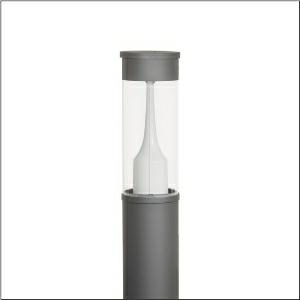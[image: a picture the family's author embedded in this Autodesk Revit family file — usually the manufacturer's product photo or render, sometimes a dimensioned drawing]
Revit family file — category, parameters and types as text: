
# Revit family: city-light_260_iq___p1_0a_5xa5295lf14h_3d8e
name_source: partatom
category: Lighting Fixtures
units: mm (PartAtom-declared; Revit-internal decimal feet)

## family parameters
Cut with Voids When Loaded = No
Host = Face
Light Source = No
Part Type = Normal
Room Calculation Point = No
Round Connector Dimension = Use Diameter
Shared = No

## types (1)
- --- (1 x LED, 1510 lm, 10 W, 4000K)
    Apparent Load = 10 VA
    CIE Flux Codes = 32 61 90 93 100
    Color Rendering = 70
    Color Temperature = 4000K
    Default Elevation = 1800 mm
    Description = City-Light 260 iQ, light pillar, Module 540 iQ-SR, primary light control with 3 zone facetted reflector, of plastic, silver coated, highly specular, structured, primary optical cover: cover, of PMMA, transparent, partly coated, light distribution: P1.0a, primary light characteristic: strongly asymmetric, LED, High Power LED, rated luminous flux: 1.510lm, luminous efficacy: 151lm/W, light colour: 740, colour temperature: 4000K, control gear: iQ Street-Remote, control: pre-setting: logarithmic dimming characteristic, Street-Remote, Auto-Match, Temp-Guard, Lumen-Switch, Night-Set, Smart-Wire, Light-Fading, Desk-Remote (wireless, voltage-free reading and setting of iQ features in the workshop via application-optimized NFC function/RFID function), optimised constant luminous flux control (CLO 2.0), with terminal, 6-pole, max. 2.5mm², mains connection: 230..240V, AC, 50/60Hz, start of lifetime: 10W, end of service life: 10W, reduction: 5W, luminaire housing, cylindrical, of extruded aluminium section, coated, Siteco® metallic grey (DB 702S), length: 2.600mm, diameter: 200mm, Module 540 iQ-SR, traffic white (RAL 9016), equipment: standard, protection rating (complete): IP65, insulation class (complete): insulation class II (safety insulation), certification: CE, ENEC, VDE, packaging unit: 1 piece

Light Distribution: P1.0a
    Height = 500 mm
    Lamp = 1 x LED
    Lamp Light Flux = 1510 lm
    Lamp Power = 10 W
    Lamp count = 1
    Length = 200 mm  [stored 0.656168 ft]
    Luminous efficacy = 151 lm/W
    Manufacturer = Siteco
    ModVariant = No
    Model = 5XA5295LF14H
    Mounting Place = Floor
    Mounting Type = Freestanding
    Number of Poles = 1
    OnlyDefault = Yes
    Power Factor = 1
    Product Name = City-Light 260 iQ | P1.0a
    Product group = light pillar
    ProductGroupID = 1301
    Protection Class = Protection class II
    Protection Degree = IP 65
    RLX_Detail_Level = 1
    RLX_Emergency_Light_Flux = 0 lm
    RLX_Emergency_Type = 0
    RLX_Emergency_Type_DB = No
    RlxData = <blob elided: 56909 chars, md5=47f50f19>
    Socket = socket
    Standby Power = 0 W
    System Light Flux = 1510 lm
    System Power = 10 W
    Type Comments = factory setting: luminous flux: 100 % | dim-lin: 254 | 401 mA
    Type Image = l_1006918.jpg
    URL = http://relux.com
    VarID = @adj_180931
    Voltage = 0 V
    Weight = 0.00 kg
    Width = 0 mm  [stored 0 ft]

note: [stored X ft] marks values corroborated as IEEE doubles in the binary element streams (Revit-internal decimal feet)

## geometry (parser evidence)
native form markers: Blend x4, Sweep x12
no freeform markers — native parametric forms only
